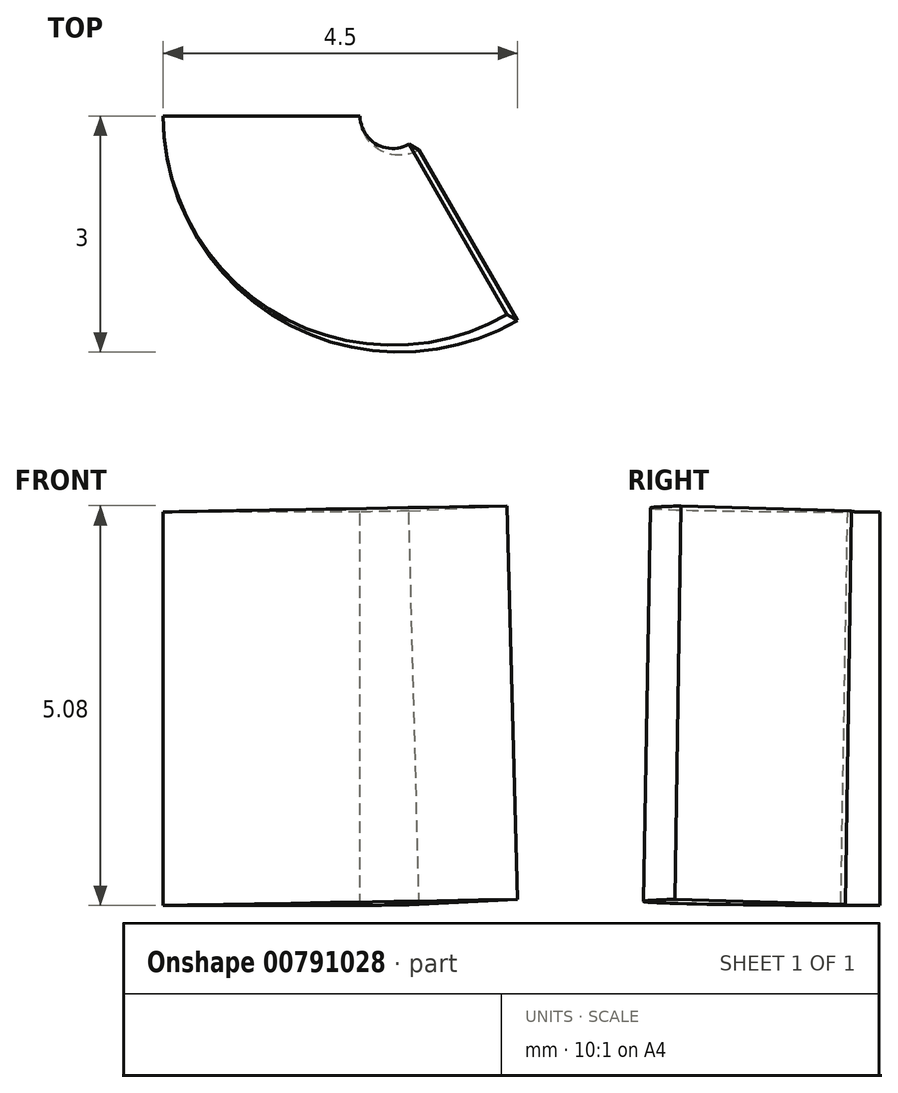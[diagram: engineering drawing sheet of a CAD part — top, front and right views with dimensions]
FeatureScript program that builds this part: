
annotation { "Feature Type Name" : "Feature", "Feature Type Description" : "" }
export const myFeature = defineFeature(function(context is Context, id is Id, definition is map)
    precondition{}
    {
        {
            var Q0;
            Q0=qCreatedBy(makeId("Front.planeOp"),FACE);
            var sketch = newSketch(context, id + "F0", { "sketchPlane" : qUnion([Q0])});
            skLineSegment(sketch, "E0.bottom", {"start": v(0, 0) * mm, "end": v(-2.5, 0) * mm});
            skLineSegment(sketch, "E0.top", {"start": v(0, 5) * mm, "end": v(-2.5, 5) * mm});
            skLineSegment(sketch, "E0.left", {"start": v(0, 0) * mm, "end": v(0, 5) * mm});
            skLineSegment(sketch, "E0.right", {"start": v(-2.5, 0) * mm, "end": v(-2.5, 5) * mm});
            skLineSegment(sketch, "E1", {"start": v(0, 0) * mm, "end": v(0.5, 0) * mm});
            skLineSegment(sketch, "E2", {"start": v(0.5, 0) * mm, "end": v(0, 28.73) * mm});
            skSolve(sketch);
        }
        {
            var Q0;
            Q0 = qSketchRegion(id + "F0", true);
            var Q1;
            Q1=sQuery(id+"F0.wireOp",EDGE,"E2");
            revolve(context, id + "F1", {"surfaceOperationType" : NewSurfaceOperationType.NEW, "entities" : qUnion([Q0]), "axis" : qUnion([Q1]), "revolveType" : RevolveType.ONE_DIRECTION, "angle" : 120 * degree});
        }
    });
